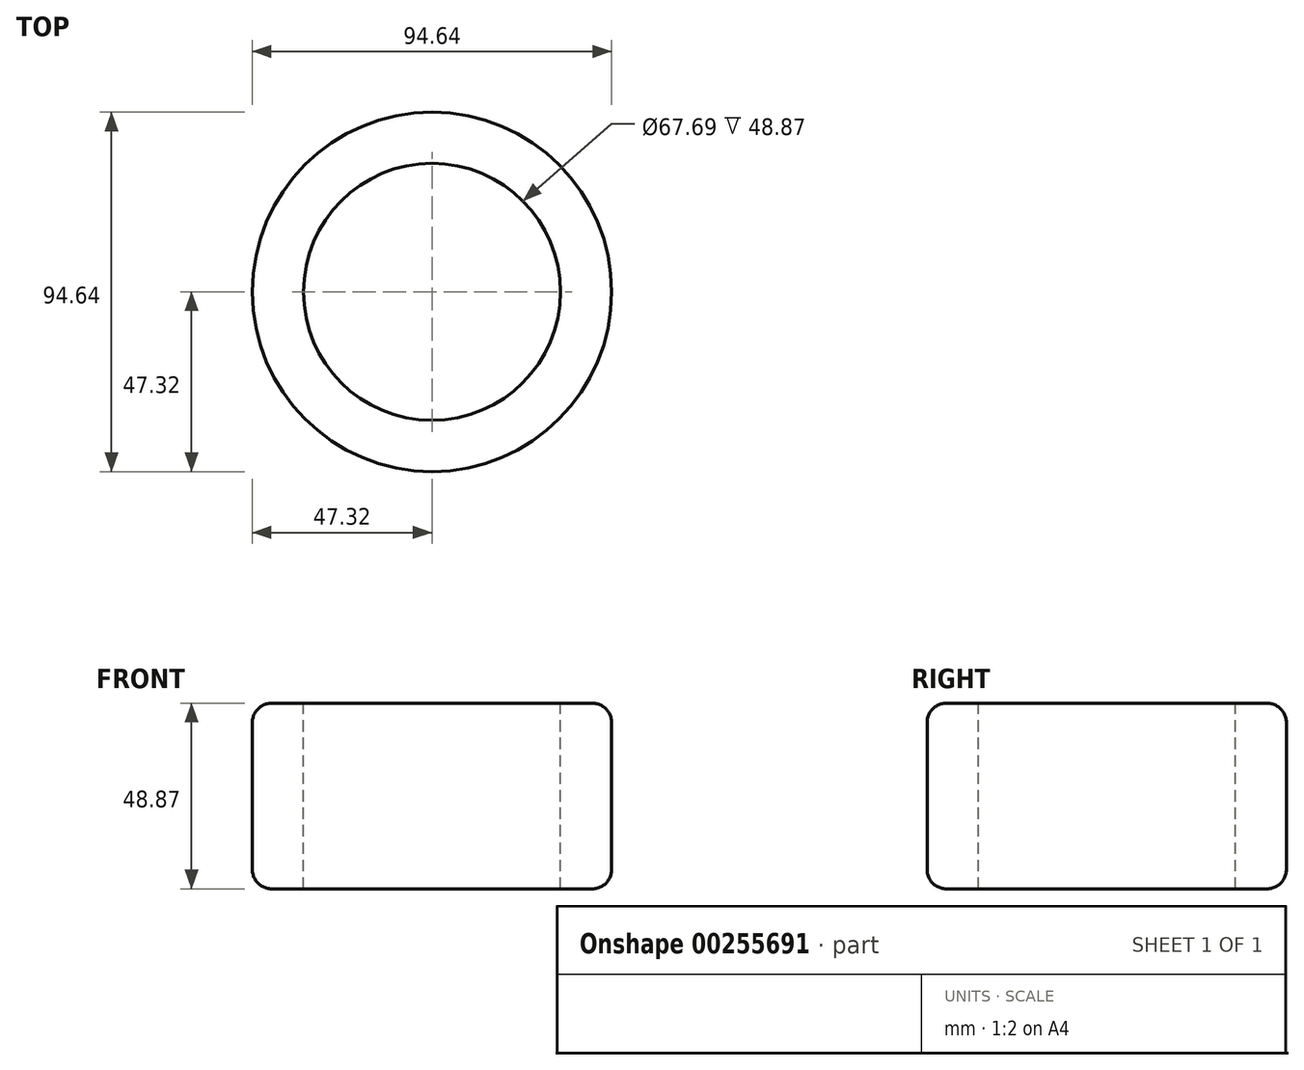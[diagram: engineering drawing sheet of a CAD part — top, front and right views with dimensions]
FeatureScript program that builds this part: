
annotation { "Feature Type Name" : "Feature", "Feature Type Description" : "" }
export const myFeature = defineFeature(function(context is Context, id is Id, definition is map)
    precondition{}
    {
        {
            var Q0;
            Q0=qCreatedBy(makeId("Front.planeOp"),FACE);
            var sketch = newSketch(context, id + "F0", { "sketchPlane" : qUnion([Q0])});
            skLineSegment(sketch, "E0.bottom", {"start": v(-47.32, 25.13) * mm, "end": v(-33.84, 25.13) * mm});
            skLineSegment(sketch, "E0.top", {"start": v(-47.32, -23.74) * mm, "end": v(-33.84, -23.74) * mm});
            skLineSegment(sketch, "E0.left", {"start": v(-47.32, 25.13) * mm, "end": v(-47.32, -23.74) * mm});
            skLineSegment(sketch, "E0.right", {"start": v(-33.84, 25.13) * mm, "end": v(-33.84, -23.74) * mm});
            skSolve(sketch);
        }
        {
            var Q0;
            Q0=qCreatedBy(makeId("Front.planeOp"),FACE);
            var sketch = newSketch(context, id + "F1", { "sketchPlane" : qUnion([Q0])});
            skLineSegment(sketch, "E1", {"start": v(0, 42.97) * mm, "end": v(0, -40.38) * mm});
            skSolve(sketch);
        }
        {
            var Q0;
            Q0=makeQuery(id+"F0.imprint","IMPRINT",FACE,{"disambiguationData":[TD([[makeQuery(id+"F0.imprint","IMPRINT",EDGE,{"derivedFrom":sQuery(id+"F0.wireOp",EDGE,"E0.bottom")}),-1.0]])]});
            var Q1;
            Q1=sQuery(id+"F1.wireOp",EDGE,"E1");
            revolve(context, id + "F2", {"entities" : qUnion([Q0]), "axis" : qUnion([Q1]), "revolveType" : RevolveType.FULL});
        }
        {
            var Q0;
            Q0=makeQuery(id+"F2.opRevolve","SWEPT_EDGE",EDGE,{"disambiguationData":[OSD([sQuery(id+"F0.wireOp",EDGE,"E0.bottom"),sQuery(id+"F0.wireOp",EDGE,"E0.left")])]});
            var Q1;
            Q1=makeQuery(id+"F2.opRevolve","SWEPT_EDGE",EDGE,{"disambiguationData":[OSD([sQuery(id+"F0.wireOp",EDGE,"E0.top"),sQuery(id+"F0.wireOp",EDGE,"E0.left")])]});
            fillet(context, id + "F3", {"entities" : qUnion([Q0, Q1]), "radius" : 5.08 * mm, "tangentPropagation" : true, "allowEdgeOverflow" : false});
        }
    });
